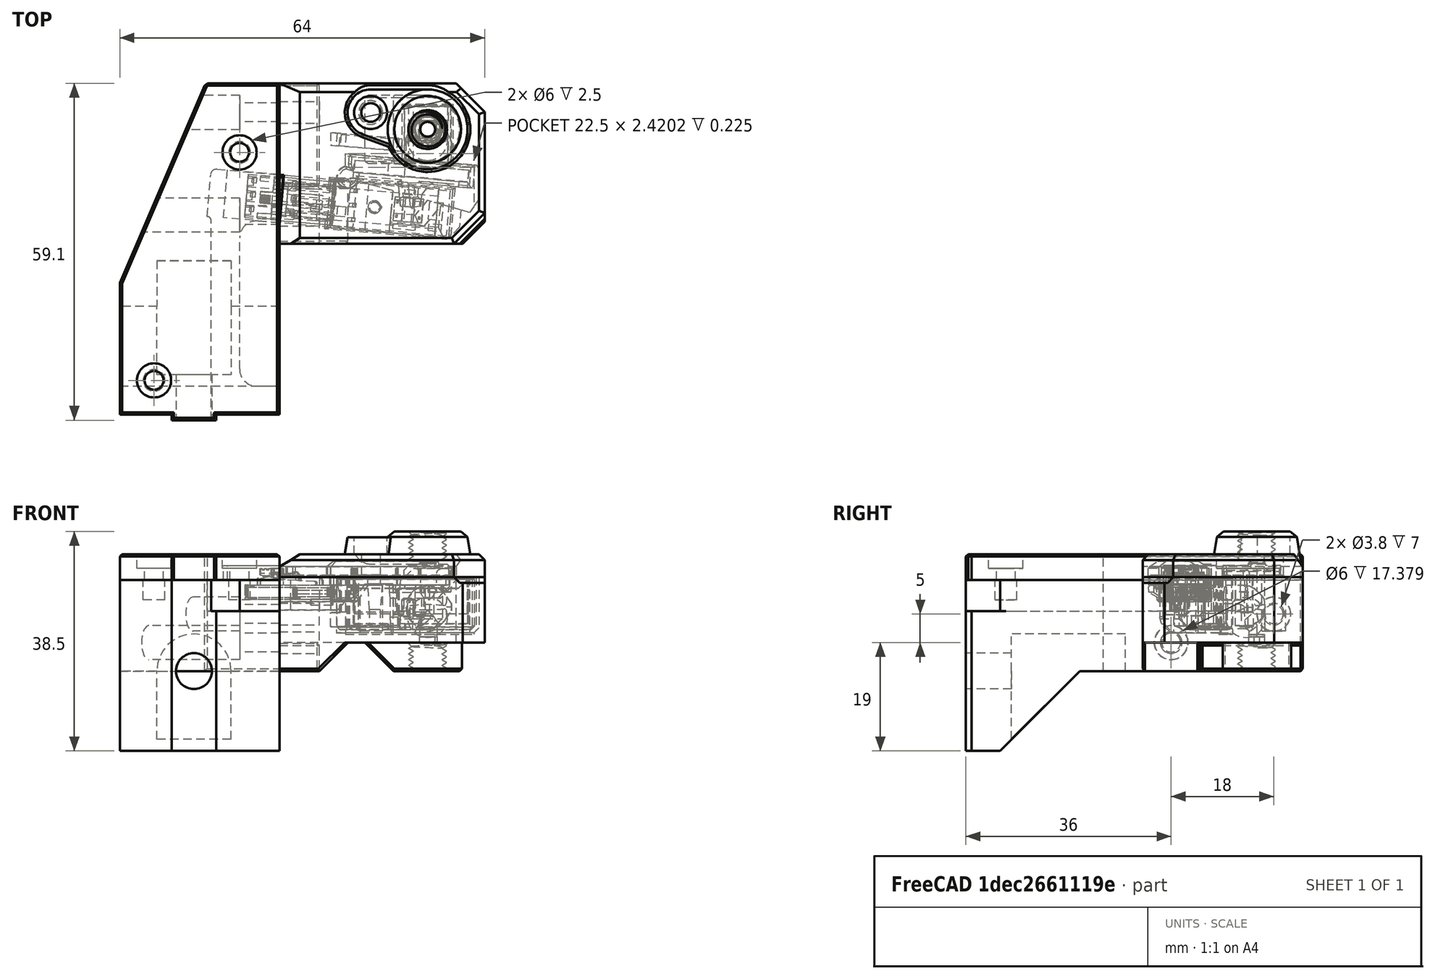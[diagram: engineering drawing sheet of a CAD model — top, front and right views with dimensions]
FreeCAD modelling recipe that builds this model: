
FCSTD DOCUMENT  (FreeCAD 0.19R24291 (Git))
Label: bear-filament-sensor-assembly
License: Other
LicenseURL: GPL3
objects: Part::Feature×11, Part::MultiFuse×2, Part::Cut×2, Part::Cylinder×2, App::Part×1, Part::Box×1, Part::Refine×1
note: 19 computed .brp shape members not serialized (recipe doc carries the construction recipe); baked Part::Feature solids carry a one-line shape summary decoded from their .brp

FEATURE [Part::Feature] Chamfer003001  label="Chamfer012"
  shape: bbox 36.01 x 28.11 x 18.46 mm, 152 faces (baked)
FEATURE [Part::Feature] Chamfer005001  label="Chamfer011"
  shape: bbox 36 x 28.1 x 8.302 mm, 88 faces (baked)
FEATURE [Part::Feature] Cut008004003004014002002005003004003002003021020001  label="Cut008004003004014002002005003004003002003021024"
  shape: bbox 35 x 59.1 x 30 mm, 60 faces (baked)
FEATURE [Part::Feature] Cut008004003004014002002005003004003002003021022001  label="Cut008004003004014002002005003004003002003021023"
  shape: bbox 28 x 59.1 x 3 mm, 32 faces (baked)
FEATURE [Part::Feature] Part__Feature032001  label="fs_lever001"
  shape: bbox 24.12 x 9.285 x 8.809 mm, 52 faces (baked)
FEATURE [Part::Feature] Part__Feature043001  label="magnet_20x6x2 v002"
  shape: bbox 20.1 x 3.736 x 6 mm, 6 faces (baked)
FEATURE [Part::Feature] Part__Feature044001  label="magnet_10x6x2 v002"
  shape: bbox 10.14 x 2.864 x 6 mm, 6 faces (baked)
FEATURE [Part::Feature] Part__Feature045001  label="steel_ball v002"
  shape: bbox 7 x 7 x 7 mm, 1 faces (baked)
FEATURE [Part::Feature] Fusion001001  label="Fusion002011011013004002017"
  shape: bbox 36.02 x 10.86 x 8.121 mm, 301 faces (baked)
FEATURE [Part::Feature] Cut008004003004014002002005003004003002003021022001001
  Placement = pos=(0,0,1.5) rot=(0,0,1;0rad)
  shape: bbox 28 x 59.1 x 3 mm, 32 faces (baked)
FEATURE [App::Part] Part  label="filament-sensor"
  Group = -> [Chamfer003001,Chamfer005001,Cut008004003004014002002005003004003002003021020001,Cut008004003004014002002005003004003002003021022001,Part__Feature032001,Part__Feature043001,Part__Feature044001,Part__Feature045001,Fusion001001,Cut008004003004014002002005003004003002003021022001001]
  Origin = -> Origin
FEATURE [Part::MultiFuse] Fusion
  Shapes = -> [Cut008004003004014002002005003004003002003021022001,Cut008004003004014002002005003004003002003021022001001]
FEATURE [Part::Box] Box  label="Cube"
  AttacherType = Attacher::AttachEngine3D
  Height = 8
  Length = 10
  Placement = pos=(-9.85454,-9.46832,10.5) rot=(0,0,1;6.19592rad)
  Width = 8.4
FEATURE [Part::Cut] Cut
  Base = -> Fusion
  Tool = -> Box
FEATURE [Part::Cylinder] Cylinder
  Angle = 360
  AttacherType = Attacher::AttachEngine3D
  Height = 10
  Placement = pos=(-7,2,11.6) rot=(0,0,1;0rad)
  Radius = 3
FEATURE [Part::Cylinder] Cylinder001
  Angle = 360
  AttacherType = Attacher::AttachEngine3D
  Height = 10
  Placement = pos=(-22,-38,11.6) rot=(0,0,1;0rad)
  Radius = 3
FEATURE [Part::MultiFuse] Fusion001002
  Placement = pos=(0,0,6.4) rot=(0,0,1;0rad)
  Shapes = -> [Cylinder001,Cylinder]
FEATURE [Part::Cut] Cut008004003004014002002005003004003002003021022001002
  Base = -> Cut
  Tool = -> Fusion001002
FEATURE [Part::Refine] Cut008004003004014002002005003004003002003021022001002001
  Source = -> Cut008004003004014002002005003004003002003021022001002
FEATURE [Part::Feature] Cut008004003004014002002005003004003002003021022001002001001
  shape: bbox 28 x 59.1 x 4.5 mm, 36 faces (baked)
